# Revit family: Access_Cover_Square_Wall-Zurn-Z1460
name_source: partatom
category: Plumbing Fixtures
units: mm (PartAtom-declared; Revit-internal decimal feet)

## family parameters
Cut with Voids When Loaded = No
Host = Face
Maintain Annotation Orientation = No
OmniClass Number = 23.30.10.27.14
OmniClass Title = Access Panels
Part Type = Normal
Room Calculation Point = No
Round Connector Dimension = Use Radius
Shared = No

## types (8) — shared parameters
Assembly Code = D2030300
CW Connection = No
Default Elevation = 20 "
Description = SQUARE WALL ACCESS COVER
HW Connection = No
Main Material = Bronze - Zurn - Polished Nickel
Manufacturer = Zurn Water, LLC
Manufacurer Brand = Zurn
Model = Z1460
Modified Date = 02/10/2026
Product Documentation Link = https://files.zurn.com
Product Page URL = https://www.zurn.com
Product data url = https://www.bimobject.com
URL = www.zurn.com
Vent Connection = No
WFU = 1
Waste Connection = Yes
zero-valued in all types: CWFU, HWFU

## per-type parameters (varying)
| type | Approx. Weight (Lbs) | Cover Material | Frame Size_A | Opening Size_C | Type Comments |
| ZANB1460 7x7 | 3 " | Steel - Zurn - Stainless - Type - 304 | 7 " | 6 " | ZANB1460 7 Inch Square Frame |
| ZANB1460 9x9 | 5 " | Steel - Zurn - Stainless - Type - 304 | 9 " | 8 " | ZANB1460 9 Inch Square Frame |
| ZANB1460 10x10 | 7 " | Steel - Zurn - Stainless - Type - 304 | 10 " | 9 " | ZANB1460 10 Inch Square Frame |
| ZANB1460 11x11 | 10 " | Steel - Zurn - Stainless - Type - 304 | 11 " | 10 " | ZANB1460 11 Inch Square Frame |
| ZAB1460 7x7 | 3 " | Bronze - Zurn - Polished | 7 " | 6 " | ZAB1460 7Inch Square Frame |
| ZAB1460 9x9 | 5 " | Bronze - Zurn - Polished | 9 " | 8 " | ZAB1460 9 Inch Square Frame |
| ZAB1460 10x10 | 7 " | Bronze - Zurn - Polished | 10 " | 9 " | ZAB1460 10 Inch Square Frame |
| ZAB1460 11x11 | 10 " | Bronze - Zurn - Polished | 11 " | 10 " | ZAB1460 11 Inch Square Frame |

## geometry (parser evidence)
native form markers: Blend x12, Sweep x2
no freeform markers — native parametric forms only
